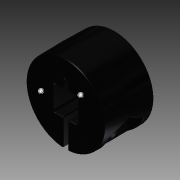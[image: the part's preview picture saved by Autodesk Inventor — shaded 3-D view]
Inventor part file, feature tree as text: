
AUTODESK INVENTOR PART (.ipt)
format: ipt  version: 2015 (Build 190159000, 159)  size: 481,280 bytes
history: native  units: in
note: dims shown in document units (in); Inventor stores cm internally (conversion verified against a paired STEP export)
features: other x2, fillet x1, imported_body x1
ambient origin geometry x8: Origin, YZ Plane, XZ Plane, XY Plane, X Axis, Y Axis, Z Axis, Center Point
bodies: Body1 (feature_tree)
feature tree (4):
  other  "Lock Collar HS (plastic)"
  fillet  "Fillet4"  [1 undecoded]
  other  "Lock Collar HS"
  imported_body  "Base1"
note: 1 required parameter value undecoded (feature->parameter linkage not recoverable at this tier; creation-order binding heuristic only, values carry confidence <= 0.55)
